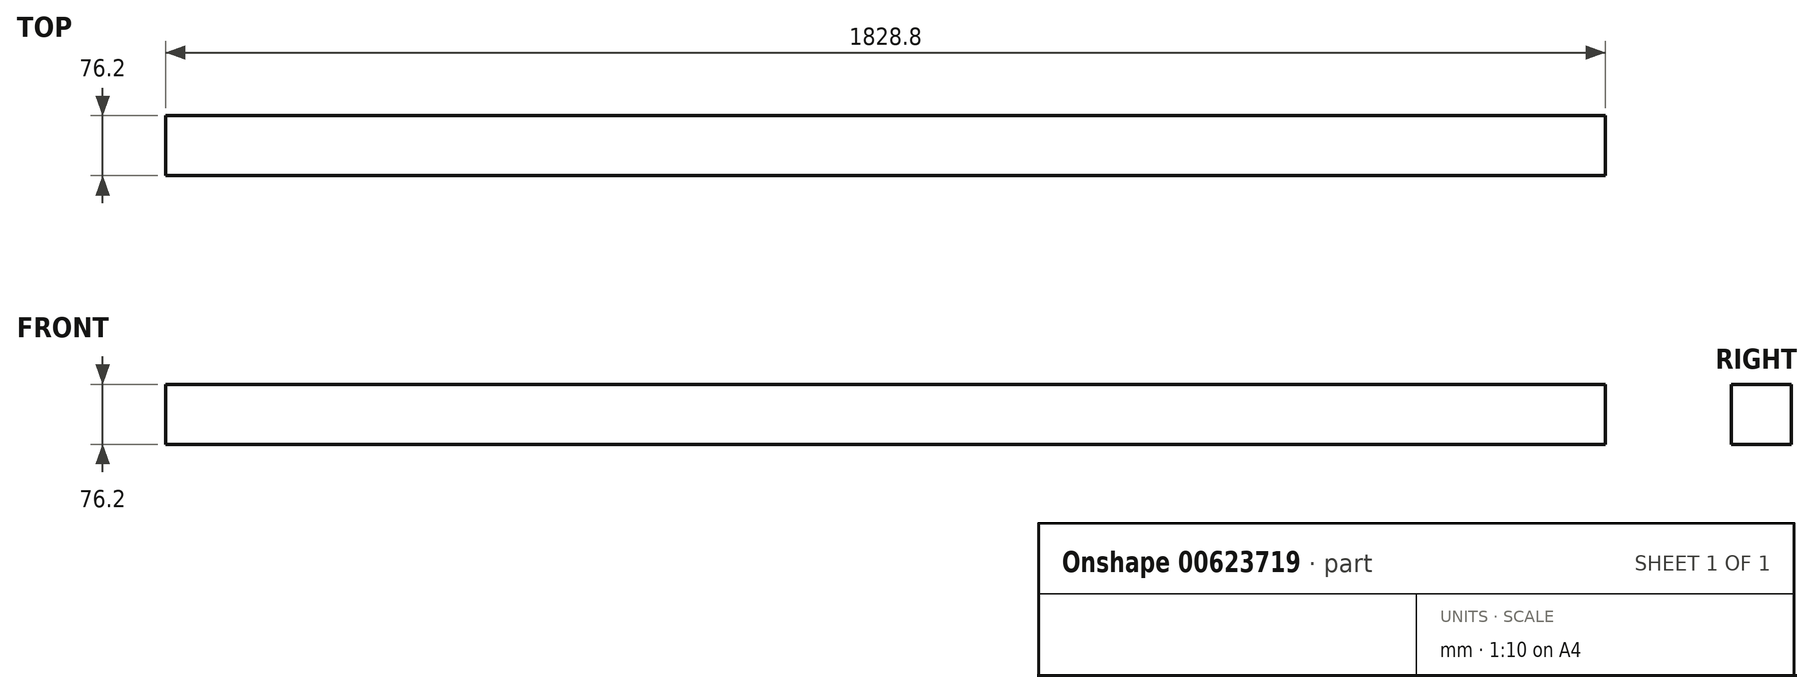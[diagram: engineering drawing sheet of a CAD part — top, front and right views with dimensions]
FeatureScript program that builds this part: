
annotation { "Feature Type Name" : "Feature", "Feature Type Description" : "" }
export const myFeature = defineFeature(function(context is Context, id is Id, definition is map)
    precondition{}
    {
        {
            var Q0;
            Q0=qCreatedBy(makeId("Front.planeOp"),FACE);
            var sketch = newSketch(context, id + "F0", { "sketchPlane" : qUnion([Q0])});
            skLineSegment(sketch, "E0.bottom", {"start": v(914.4, 38.1) * mm, "end": v(-914.4, 38.1) * mm});
            skLineSegment(sketch, "E0.top", {"start": v(914.4, -38.1) * mm, "end": v(-914.4, -38.1) * mm});
            skLineSegment(sketch, "E0.left", {"start": v(914.4, 38.1) * mm, "end": v(914.4, -38.1) * mm});
            skLineSegment(sketch, "E0.right", {"start": v(-914.4, 38.1) * mm, "end": v(-914.4, -38.1) * mm});
            skPoint(sketch, "E0.middle", {"position": v(0, 0) * mm});
            skSolve(sketch);
        }
        {
            var Q0;
            Q0 = qSketchRegion(id + "F0", true);
            extrude(context, id + "F1", {"entities" : qUnion([Q0]), "depth" : 76.2 * mm, "offsetDistance" : 25.4 * mm});
        }
    });
